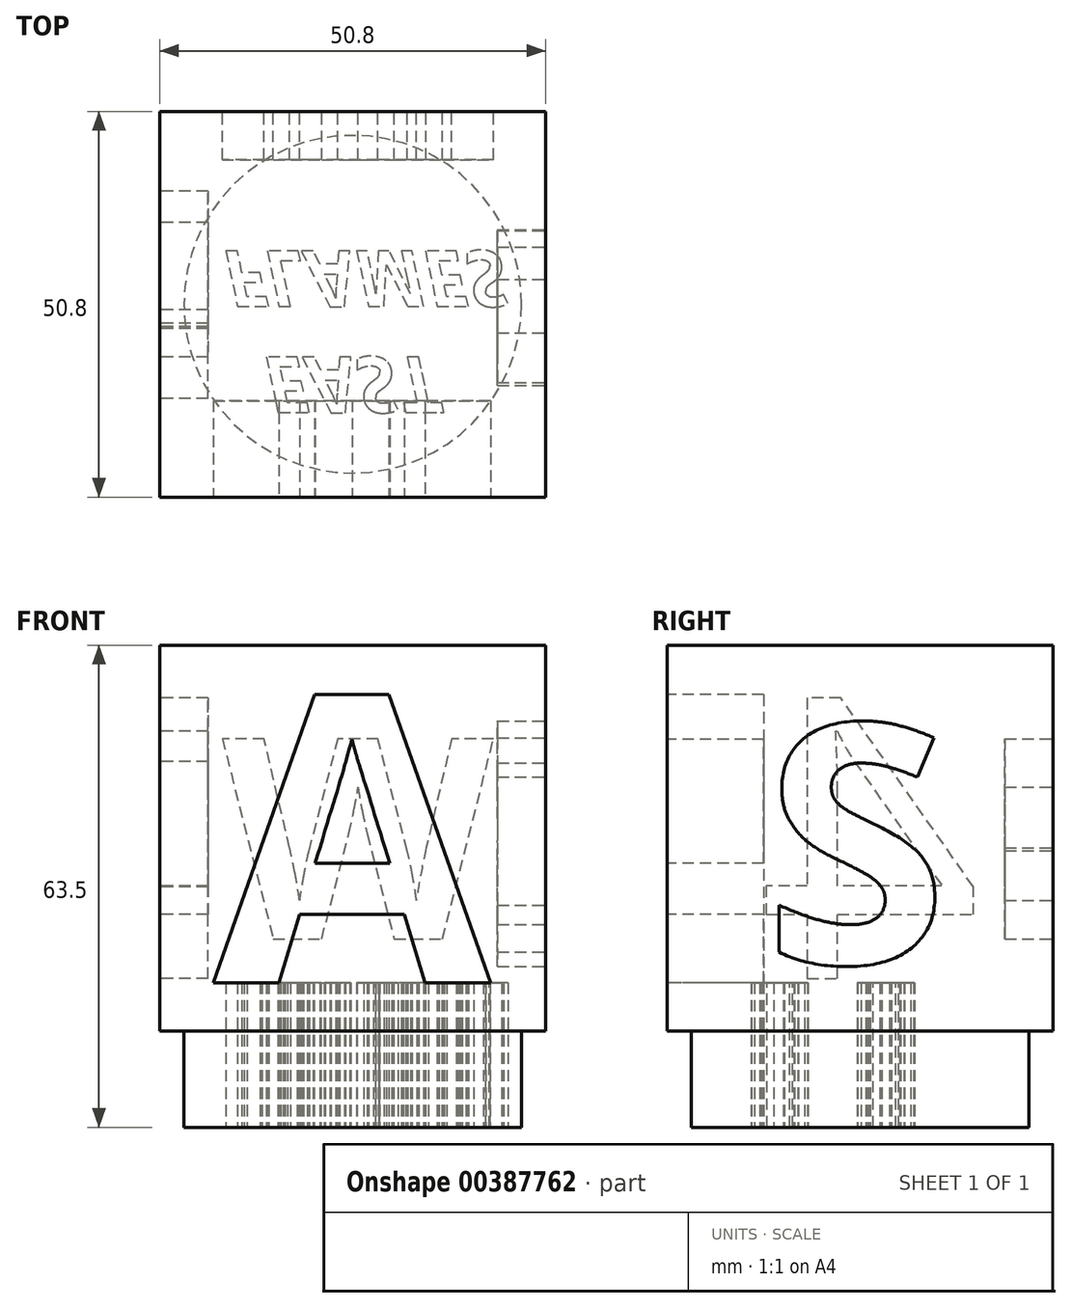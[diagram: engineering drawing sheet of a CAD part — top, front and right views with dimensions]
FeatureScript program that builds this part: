
annotation { "Feature Type Name" : "Feature", "Feature Type Description" : "" }
export const myFeature = defineFeature(function(context is Context, id is Id, definition is map)
    precondition{}
    {
        {
            var Q0;
            Q0=qCreatedBy(makeId("Front.planeOp"),FACE);
            var sketch = newSketch(context, id + "F0", { "sketchPlane" : qUnion([Q0])});
            skLineSegment(sketch, "E0", {"start": v(0, 0) * mm, "end": v(0, 50.8) * mm});
            skLineSegment(sketch, "E1", {"start": v(0, 50.8) * mm, "end": v(50.8, 50.8) * mm});
            skLineSegment(sketch, "E2", {"start": v(50.8, 50.8) * mm, "end": v(50.8, 0) * mm});
            skLineSegment(sketch, "E3", {"start": v(50.8, 0) * mm, "end": v(0, 0) * mm});
            skSolve(sketch);
        }
        {
            var Q0;
            Q0 = qSketchRegion(id + "F0", true);
            extrude(context, id + "F1", {"entities" : qUnion([Q0]), "depth" : 50.8 * mm});
        }
        {
            var Q0;
            Q0=makeQuery(id+"F1.opExtrude","CAP_FACE",FACE,{"disambiguationData":[OSD([sQuery(id+"F0.wireOp",EDGE,"E0"),sQuery(id+"F0.wireOp",EDGE,"E1"),sQuery(id+"F0.wireOp",EDGE,"E2"),sQuery(id+"F0.wireOp",EDGE,"E3")])],"isStart":false});
            var sketch = newSketch(context, id + "F2", { "sketchPlane" : qUnion([Q0])});
            skText(sketch, "E4", { "text": "A", "fontName": "OpenSans-Bold.ttf"});
            const initialGuessF2  = {"E4": [0.00705, 0.00635, 1, 0, 0.0381]};
            skSetInitialGuess(sketch, initialGuessF2);
            skSolve(sketch);
        }
        {
            var Q0;
            Q0=makeQuery(id+"F2.imprint","IMPRINT",FACE,{"disambiguationData":[TD([[makeQuery(id+"F2.imprint","IMPRINT",EDGE,{"derivedFrom":sQuery(id+"F2.wireOp",EDGE,"E4.sketch_text.stroke-0")}),-1.0]])]});
            extrude(context, id + "F3", {"entities" : qUnion([Q0]), "operationType" : NewBodyOperationType.REMOVE, "oppositeDirection" : true, "depth" : 12.7 * mm});
        }
        {
            var Q0;
            Q0=makeQuery(id+"F1.opExtrude","SWEPT_FACE",FACE,{"disambiguationData":[OSD([sQuery(id+"F0.wireOp",EDGE,"E2")])]});
            var sketch = newSketch(context, id + "F4", { "sketchPlane" : qUnion([Q0])});
            skText(sketch, "E5", { "text": "S", "fontName": "OpenSans-Bold.ttf"});
            const initialGuessF4  = {"E5": [-0.0381, 0.0089, 1, 0, 0.03174]};
            skSetInitialGuess(sketch, initialGuessF4);
            skSolve(sketch);
        }
        {
            var Q0;
            Q0 = qSketchRegion(id + "F4", true);
            extrude(context, id + "F5", {"entities" : qUnion([Q0]), "operationType" : NewBodyOperationType.REMOVE, "oppositeDirection" : true, "depth" : 6.35 * mm});
        }
        {
            var Q0;
            Q0=makeQuery(id+"F1.opExtrude","CAP_FACE",FACE,{"disambiguationData":[OSD([sQuery(id+"F0.wireOp",EDGE,"E0"),sQuery(id+"F0.wireOp",EDGE,"E1"),sQuery(id+"F0.wireOp",EDGE,"E2"),sQuery(id+"F0.wireOp",EDGE,"E3")])],"isStart":true});
            var sketch = newSketch(context, id + "F6", { "sketchPlane" : qUnion([Q0])});
            skText(sketch, "E6", { "text": "W", "fontName": "OpenSans-Bold.ttf"});
            const initialGuessF6  = {"E6": [-0.04394, 0.01212, 1, 0, 0.02659]};
            skSetInitialGuess(sketch, initialGuessF6);
            skSolve(sketch);
        }
        {
            var Q0;
            Q0 = qSketchRegion(id + "F6", true);
            extrude(context, id + "F7", {"entities" : qUnion([Q0]), "operationType" : NewBodyOperationType.REMOVE, "oppositeDirection" : true, "depth" : 6.35 * mm});
        }
        {
            var Q0;
            Q0=makeQuery(id+"F1.opExtrude","SWEPT_FACE",FACE,{"disambiguationData":[OSD([sQuery(id+"F0.wireOp",EDGE,"E0")])]});
            var sketch = newSketch(context, id + "F8", { "sketchPlane" : qUnion([Q0])});
            skText(sketch, "E7", { "text": "4", "fontName": "OpenSans-Regular.ttf"});
            const initialGuessF8  = {"E7": [0.0094, 0.00687, 1, 0, 0.03708]};
            skSetInitialGuess(sketch, initialGuessF8);
            skSolve(sketch);
        }
        {
            var Q0;
            Q0 = qSketchRegion(id + "F8", true);
            extrude(context, id + "F9", {"entities" : qUnion([Q0]), "operationType" : NewBodyOperationType.REMOVE, "oppositeDirection" : true, "depth" : 6.35 * mm});
        }
        {
            var Q0;
            Q0=makeQuery(id+"F1.opExtrude","SWEPT_FACE",FACE,{"disambiguationData":[OSD([sQuery(id+"F0.wireOp",EDGE,"E3")])]});
            var sketch = newSketch(context, id + "F10", { "sketchPlane" : qUnion([Q0])});
            skCircle(sketch, "E8", {"center": v(25.4, 25.4) * mm, "radius": 22.23 * mm});
            skPoint(sketch, "E8.centerSnap0", {"position": v(0, 25.4) * mm});
            skPoint(sketch, "E8.centerSnap1", {"position": v(25.4, 0) * mm});
            skSolve(sketch);
        }
        {
            var Q0;
            Q0 = qSketchRegion(id + "F10", true);
            extrude(context, id + "F11", {"entities" : qUnion([Q0]), "operationType" : NewBodyOperationType.ADD, "depth" : 12.7 * mm});
        }
        {
            var Q0;
            Q0=makeQuery(id+"F11.opExtrude","CAP_FACE",FACE,{"disambiguationData":[OSD([sQuery(id+"F10.wireOp",EDGE,"E8")])],"isStart":false});
            var sketch = newSketch(context, id + "F12", { "sketchPlane" : qUnion([Q0])});
            skText(sketch, "E9", { "text": "  EAST\nFLAMES", "fontName": "OpenSans-BoldItalic.ttf"});
            const initialGuessF12  = {"E9": [0.00842, 0.03233, 1, 0, 0.0074]};
            skSetInitialGuess(sketch, initialGuessF12);
            skSolve(sketch);
        }
        {
            var Q0;
            Q0 = qSketchRegion(id + "F12", true);
            extrude(context, id + "F13", {"entities" : qUnion([Q0]), "operationType" : NewBodyOperationType.REMOVE, "oppositeDirection" : true, "depth" : 19.05 * mm});
        }
        {
            var Q0;
            Q0 = qSketchRegion(id + "F12", true);
            extrude(context, id + "F14", {"entities" : qUnion([Q0]), "operationType" : NewBodyOperationType.REMOVE, "oppositeDirection" : true, "depth" : 12.7 * mm});
        }
    });
